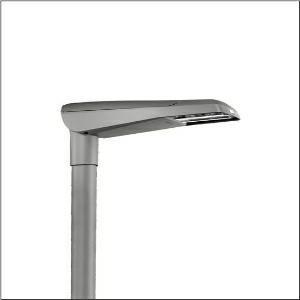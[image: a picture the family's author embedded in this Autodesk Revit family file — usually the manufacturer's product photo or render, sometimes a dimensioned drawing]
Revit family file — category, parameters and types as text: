
# Revit family: streetlight_sl_11_iq_micro___st1_2a_5xc1ac1g08de_fbfe
name_source: partatom
category: Lighting Fixtures
units: mm (PartAtom-declared; Revit-internal decimal feet)

## family parameters
Cut with Voids When Loaded = No
Host = Face
Light Source = No
Part Type = Normal
Room Calculation Point = No
Round Connector Dimension = Use Diameter
Shared = No

## types (1)
- --- (1 x LED, 3860 lm, 27.4 W, 4000K)
    Apparent Load = 27 VA
    CIE Flux Codes = 33 71 96 100 100
    Color Rendering = 70
    Color Temperature = 4000K
    Default Elevation = 1800 mm
    Description = Streetlight SL 11 iQ micro, mast luminaire, primary light control with 3 zone facetted reflector, of plastic, silver coated, highly specular, primary optical cover: cover, of PMMA, transparent, light distribution: ST1.2a, light emission: direct distribution, primary light characteristic: asymmetric, installation type: post-top, side-entry, lamps: LED, High Power LED, rated values: 3.620lm | 27,7W | 130,7lm/W (begin service life); end service life: 3.620lm | 28,1W; at 50% lumin. flux: 1.810lm | 13,4W | 135,1lm/W, colour temperature: 2200/2700/3000/4000K, colour rendering: CRI > 70, light colour: 722/727/730/740, light setting 1 begin service life: 100% | 3.620lm | 27,7W | 130,7lm/W | 3.000K, light setting 1 end service life: 28,1W, further light settings possible, control: pre-setting: linear dimming characteristic, Street-Remote, Auto-Match, Temp-Guard, Lumen-Switch, Night-Set, Smart-Wire, Light-Fading, Desk-Remote (wireless, voltage-free reading and setting of iQ features in the workshop via application-optimized NFC function/RFID function), optimised constant luminous flux control (CLO 2.0), with cable H07RN-F 5x 1.5mm², mains connection: 220..240V, AC, 50/60Hz, connection cable pre-assembled, cable length: 6,5m, luminaire housing, of diecast aluminium, powder-coated, SITECO metallic grey (DB 702S), please order mast flange separately, inclination adjustable without tools: 0°, 5°, 10°, 15° (post-top) | 0°, -5°, -10°, -15° (side-entry), sealing non-destructively replaceable, multi-level sealing system, length: 600mm, width: 174mm, height: 116mm, mast flange for spigot size: 42mm (side-entry): 5XC10008XM4, 60/48mm (side-entry/post-top): 5XC10108XM2, 76/60mm (side-entry/post-top): 5XC10108XM1, equipment: Power, protection rating (complete): IP66, insulation class (complete): insulation class II (safety insulation), certification: CE, ENEC, ENEC+, VDE, impact resistance: IK10, permissible operating ambient temperature for outdoor applications: -25..+50°C, standard-compliant lighting for roads and squares, Environmental Product Declaration (EPD) tested and certified by an independent institute, packaging unit: 1 piece

Light Distribution: ST1.2a
    Height = 116 mm
    Lamp = 1 x LED
    Lamp Light Flux = 3860 lm
    Lamp Power = 27.4 W
    Lamp count = 1
    Length = 600 mm
    Luminous efficacy = 141 lm/W
    Manufacturer = Siteco
    ModVariant = No
    Model = 5XC1AC1G08DE
    Number of Poles = 1
    OnlyDefault = Yes
    Power Factor = 1
    Product Name = Streetlight SL 11 iQ micro | ST1.2a
    Product group = mast luminaire | pylon top
    ProductGroupID = 6100
    Protection Class = Protection class II
    Protection Degree = IP 66
    RLX_Detail_Level = 1
    RLX_Emergency_Light_Flux = 0 lm
    RLX_Emergency_Type = 0
    RLX_Emergency_Type_DB = No
    RlxData = <blob elided: 59629 chars, md5=cc939dd4>
    Socket = socket
    Standby Power = 0 W
    System Light Flux = 3860 lm
    System Power = 27 W
    Type Comments = individual setting: luminous flux: 100 % | dim-lin: 254 | 726 mA
    Type Image = l_1006566.jpg
    URL = http://relux.com
    VarID = @adj_047325
    Voltage = 0 V
    Weight = 0.00 kg
    Width = 174 mm

## geometry (parser evidence)
native form markers: Blend x4, Sweep x10
no freeform markers — native parametric forms only
